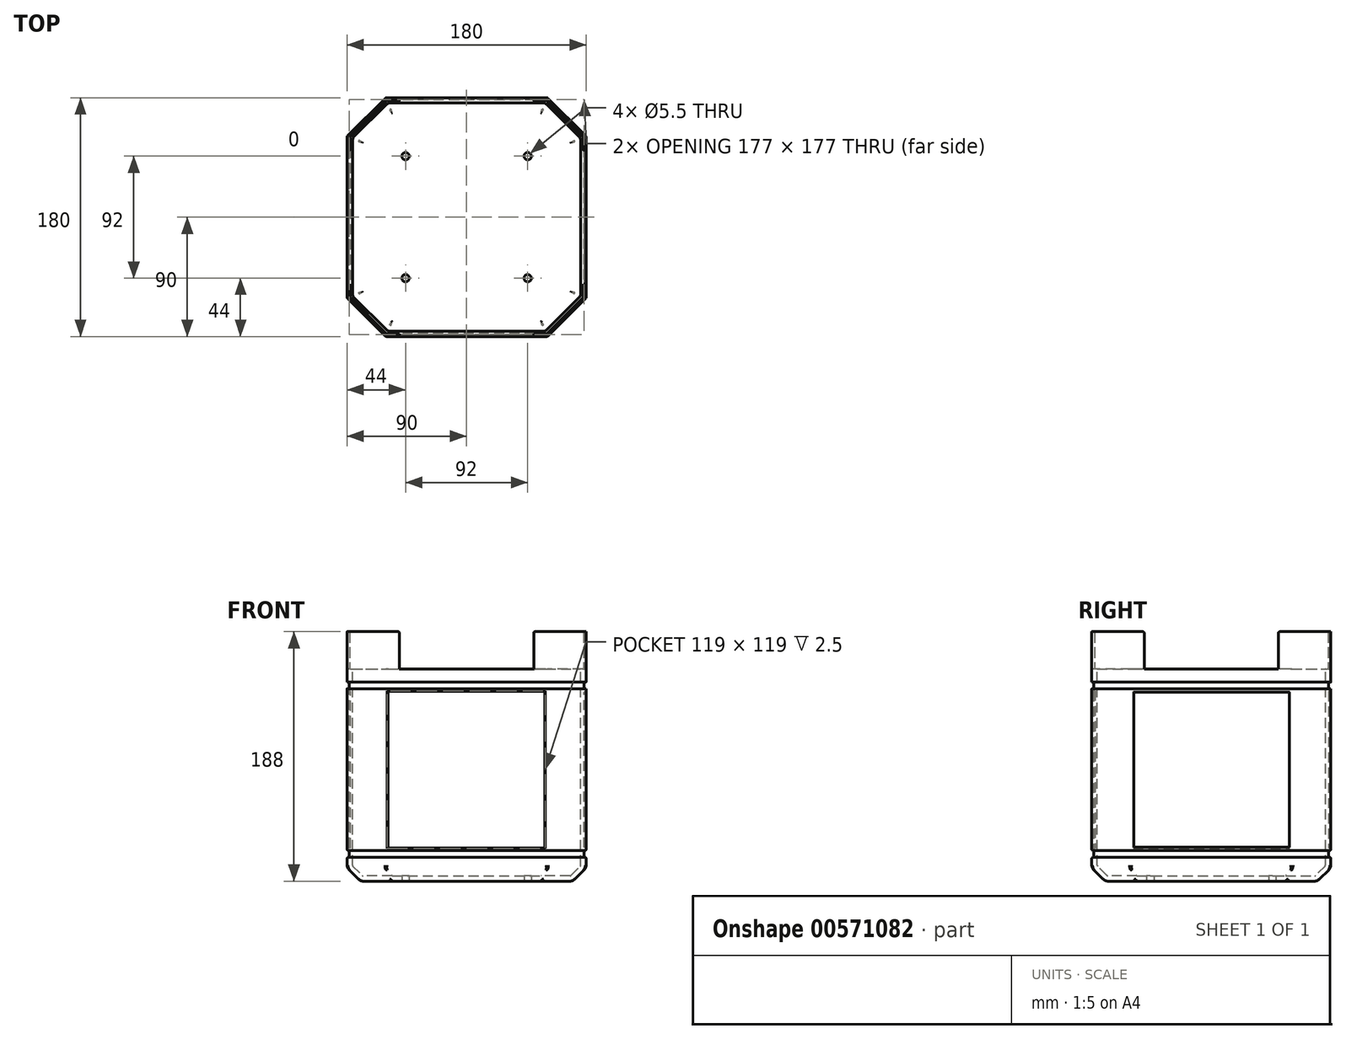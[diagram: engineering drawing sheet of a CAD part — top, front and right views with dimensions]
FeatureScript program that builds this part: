
annotation { "Feature Type Name" : "Feature", "Feature Type Description" : "" }
export const myFeature = defineFeature(function(context is Context, id is Id, definition is map)
    precondition{}
    {
        {
            var Q0;
            Q0=qCreatedBy(makeId("Top.planeOp"),FACE);
            var sketch = newSketch(context, id + "F0", { "sketchPlane" : qUnion([Q0])});
            skLineSegment(sketch, "E0.bottom", {"start": v(-61, 90) * mm, "end": v(61, 90) * mm});
            skLineSegment(sketch, "E0.top", {"start": v(-61, -90) * mm, "end": v(61, -90) * mm});
            skLineSegment(sketch, "E0.left", {"start": v(-90, 61) * mm, "end": v(-90, -61) * mm});
            skLineSegment(sketch, "E0.right", {"start": v(90, 61) * mm, "end": v(90, -61) * mm});
            skLineSegment(sketch, "E1", {"start": v(0, 156.9) * mm, "end": v(0, -146.72) * mm, "construction": true});
            skLineSegment(sketch, "E2", {"start": v(-149.43, 0) * mm, "end": v(169.81, 0) * mm, "construction": true});
            skLineSegment(sketch, "E3", {"start": v(-90, 61) * mm, "end": v(-61, 90) * mm});
            skLineSegment(sketch, "E4", {"start": v(-90, -61) * mm, "end": v(-61, -90) * mm});
            skLineSegment(sketch, "E5", {"start": v(61, -90) * mm, "end": v(90, -61) * mm});
            skLineSegment(sketch, "E6", {"start": v(61, 90) * mm, "end": v(90, 61) * mm});
            skPoint(sketch, "E7.orphan", {"position": v(-90, 90) * mm});
            skPoint(sketch, "E8.orphan", {"position": v(90, 90) * mm});
            skPoint(sketch, "E9.orphan", {"position": v(90, -90) * mm});
            skPoint(sketch, "E10.orphan", {"position": v(-90, -90) * mm});
            skSolve(sketch);
        }
        {
            var Q0;
            Q0=qSketchRegion(id+"F0",true);
            extrude(context, id + "F1", {"entities" : qUnion([Q0]), "depth" : 160 * mm, "offsetDistance" : 25 * mm});
        }
        {
            var Q0;
            Q0=makeQuery(id+"F1.opExtrude","CAP_EDGE",EDGE,{"disambiguationData":[OSD([sQuery(id+"F0.wireOp",EDGE,"E0.top")])],"isStart":true});
            var Q1;
            Q1=makeQuery(id+"F1.opExtrude","CAP_EDGE",EDGE,{"disambiguationData":[OSD([sQuery(id+"F0.wireOp",EDGE,"E4")])],"isStart":true});
            var Q2;
            Q2=makeQuery(id+"F1.opExtrude","CAP_EDGE",EDGE,{"disambiguationData":[OSD([sQuery(id+"F0.wireOp",EDGE,"E0.left")])],"isStart":true});
            var Q3;
            Q3=makeQuery(id+"F1.opExtrude","CAP_EDGE",EDGE,{"disambiguationData":[OSD([sQuery(id+"F0.wireOp",EDGE,"E3")])],"isStart":true});
            var Q4;
            Q4=makeQuery(id+"F1.opExtrude","CAP_EDGE",EDGE,{"disambiguationData":[OSD([sQuery(id+"F0.wireOp",EDGE,"E0.bottom")])],"isStart":true});
            var Q5;
            Q5=makeQuery(id+"F1.opExtrude","CAP_EDGE",EDGE,{"disambiguationData":[OSD([sQuery(id+"F0.wireOp",EDGE,"E6")])],"isStart":true});
            var Q6;
            Q6=makeQuery(id+"F1.opExtrude","CAP_EDGE",EDGE,{"disambiguationData":[OSD([sQuery(id+"F0.wireOp",EDGE,"E0.right")])],"isStart":true});
            var Q7;
            Q7=makeQuery(id+"F1.opExtrude","CAP_EDGE",EDGE,{"disambiguationData":[OSD([sQuery(id+"F0.wireOp",EDGE,"E5")])],"isStart":true});
            chamfer(context, id + "F2", {"entities" : qUnion([Q0, Q1, Q2, Q3, Q4, Q5, Q6, Q7]), "chamferType" : ChamferType.TWO_OFFSETS, "width1" : 10 * mm, "oppositeDirection" : true, "width2" : 10 * mm, "tangentPropagation" : true});
        }
        {
            var Q0;
            Q0=makeQuery(id+"F1.opExtrude","CAP_FACE",FACE,{"disambiguationData":[OSD([sQuery(id+"F0.wireOp",EDGE,"E0.bottom"),sQuery(id+"F0.wireOp",EDGE,"E0.top"),sQuery(id+"F0.wireOp",EDGE,"E0.left"),sQuery(id+"F0.wireOp",EDGE,"E0.right"),sQuery(id+"F0.wireOp",EDGE,"E3"),sQuery(id+"F0.wireOp",EDGE,"E4"),sQuery(id+"F0.wireOp",EDGE,"E5"),sQuery(id+"F0.wireOp",EDGE,"E6")])],"isStart":false});
            var sketch = newSketch(context, id + "F3", { "sketchPlane" : qUnion([Q0])});
            skLineSegment(sketch, "E11", {"start": v(90, -61) * mm, "end": v(61, -90) * mm});
            skLineSegment(sketch, "E12.0", {"start": v(88, -60.17) * mm, "end": v(60.17, -88) * mm});
            skLineSegment(sketch, "E13", {"start": v(90, -61) * mm, "end": v(90, -90) * mm, "construction": true});
            skLineSegment(sketch, "E14", {"start": v(90, -90) * mm, "end": v(61, -90) * mm, "construction": true});
            skLineSegment(sketch, "E15", {"start": v(90, -61) * mm, "end": v(90, -50.5) * mm});
            skLineSegment(sketch, "E16", {"start": v(61, -90) * mm, "end": v(50.5, -90) * mm});
            skLineSegment(sketch, "E17.0", {"start": v(60.17, -88) * mm, "end": v(50.5, -88) * mm});
            skLineSegment(sketch, "E18.0", {"start": v(88, -60.17) * mm, "end": v(88, -50.5) * mm});
            skLineSegment(sketch, "E19", {"start": v(88, -50.5) * mm, "end": v(90, -50.5) * mm});
            skLineSegment(sketch, "E20", {"start": v(50.5, -88) * mm, "end": v(50.5, -90) * mm});
            skLineSegment(sketch, "E21", {"start": v(104.54, 0) * mm, "end": v(-130.04, 0) * mm, "construction": true});
            skPoint(sketch, "E21.endSnap0", {"position": v(-90, 0) * mm});
            skLineSegment(sketch, "E22", {"start": v(0, 121.87) * mm, "end": v(0, -139.26) * mm, "construction": true});
            skLineSegment(sketch, "E23.MirrorCS", {"start": v(88, 50.5) * mm, "end": v(90, 50.5) * mm});
            skLineSegment(sketch, "E24.MirrorCS", {"start": v(50.5, 88) * mm, "end": v(50.5, 90) * mm});
            skLineSegment(sketch, "E25.MirrorCS", {"start": v(61, 90) * mm, "end": v(50.5, 90) * mm});
            skLineSegment(sketch, "E26.MirrorCS", {"start": v(60.17, 88) * mm, "end": v(50.5, 88) * mm});
            skLineSegment(sketch, "E27.MirrorCS", {"start": v(88, 60.17) * mm, "end": v(88, 50.5) * mm});
            skLineSegment(sketch, "E28.MirrorCS", {"start": v(90, 61) * mm, "end": v(90, 50.5) * mm});
            skLineSegment(sketch, "E29.MirrorCS", {"start": v(90, 61) * mm, "end": v(61, 90) * mm});
            skLineSegment(sketch, "E30.MirrorCS", {"start": v(88, 60.17) * mm, "end": v(60.17, 88) * mm});
            skLineSegment(sketch, "E31.MirrorCS", {"start": v(90, 90) * mm, "end": v(61, 90) * mm, "construction": true});
            skLineSegment(sketch, "E32.MirrorCS", {"start": v(90, 61) * mm, "end": v(90, 90) * mm, "construction": true});
            skLineSegment(sketch, "E33.MirrorCS", {"start": v(-88, 50.5) * mm, "end": v(-90, 50.5) * mm});
            skLineSegment(sketch, "E34.MirrorCS", {"start": v(-50.5, 88) * mm, "end": v(-50.5, 90) * mm});
            skLineSegment(sketch, "E35.MirrorCS", {"start": v(-88, -50.5) * mm, "end": v(-90, -50.5) * mm});
            skLineSegment(sketch, "E36.MirrorCS", {"start": v(-50.5, -88) * mm, "end": v(-50.5, -90) * mm});
            skLineSegment(sketch, "E37.MirrorCS", {"start": v(-61, -90) * mm, "end": v(-50.5, -90) * mm});
            skLineSegment(sketch, "E38.MirrorCS", {"start": v(-88, 60.17) * mm, "end": v(-88, 50.5) * mm});
            skLineSegment(sketch, "E39.MirrorCS", {"start": v(-61, 90) * mm, "end": v(-50.5, 90) * mm});
            skLineSegment(sketch, "E40.MirrorCS", {"start": v(-88, 60.17) * mm, "end": v(-60.17, 88) * mm});
            skLineSegment(sketch, "E41.MirrorCS", {"start": v(-88, -60.17) * mm, "end": v(-88, -50.5) * mm});
            skLineSegment(sketch, "E42.MirrorCS", {"start": v(-90, 61) * mm, "end": v(-61, 90) * mm});
            skLineSegment(sketch, "E43.MirrorCS", {"start": v(-60.17, 88) * mm, "end": v(-50.5, 88) * mm});
            skLineSegment(sketch, "E44.MirrorCS", {"start": v(-90, 61) * mm, "end": v(-90, 50.5) * mm});
            skLineSegment(sketch, "E45.MirrorCS", {"start": v(-90, -61) * mm, "end": v(-90, -50.5) * mm});
            skLineSegment(sketch, "E46.MirrorCS", {"start": v(-60.17, -88) * mm, "end": v(-50.5, -88) * mm});
            skLineSegment(sketch, "E47.MirrorCS", {"start": v(-90, 90) * mm, "end": v(-61, 90) * mm, "construction": true});
            skLineSegment(sketch, "E48.MirrorCS", {"start": v(-90, 61) * mm, "end": v(-90, 90) * mm, "construction": true});
            skLineSegment(sketch, "E49.MirrorCS", {"start": v(-90, -61) * mm, "end": v(-61, -90) * mm});
            skLineSegment(sketch, "E50.MirrorCS", {"start": v(-90, -61) * mm, "end": v(-90, -90) * mm, "construction": true});
            skLineSegment(sketch, "E51.MirrorCS", {"start": v(-90, -90) * mm, "end": v(-61, -90) * mm, "construction": true});
            skLineSegment(sketch, "E52.MirrorCS", {"start": v(-88, -60.17) * mm, "end": v(-60.17, -88) * mm});
            skSolve(sketch);
        }
        {
            var Q0;
            Q0=qSketchRegion(id+"F3",true);
            extrude(context, id + "F4", {"entities" : qUnion([Q0]), "operationType" : NewBodyOperationType.ADD, "depth" : 28 * mm});
        }
        {
            var Q0;
            {var subQ0=sQuery(id+"F0.wireOp",EDGE,"E6");Q0=makeQuery(id+"F2.opChamfer","BLEND_EDGE",EDGE,{"blendedFrom":[makeQuery(id+"F1.opExtrude","CAP_EDGE",EDGE,{"disambiguationData":[OSD([subQ0])],"isStart":true}),makeQuery(id+"F1.opExtrude","SWEPT_FACE",FACE,{"disambiguationData":[OSD([subQ0])]})],"blendedInto":[makeQuery(id+"F1.opExtrude","SWEPT_FACE",FACE,{"disambiguationData":[OSD([subQ0])]})]});}
            var Q1;
            {var subQ0=sQuery(id+"F0.wireOp",EDGE,"E0.right");Q1=makeQuery(id+"F2.opChamfer","BLEND_EDGE",EDGE,{"blendedFrom":[makeQuery(id+"F1.opExtrude","CAP_EDGE",EDGE,{"disambiguationData":[OSD([subQ0])],"isStart":true}),makeQuery(id+"F1.opExtrude","SWEPT_FACE",FACE,{"disambiguationData":[OSD([subQ0])]})],"blendedInto":[makeQuery(id+"F1.opExtrude","SWEPT_FACE",FACE,{"disambiguationData":[OSD([subQ0])]})]});}
            var Q2;
            {var subQ0=sQuery(id+"F0.wireOp",EDGE,"E5");Q2=makeQuery(id+"F2.opChamfer","BLEND_EDGE",EDGE,{"blendedFrom":[makeQuery(id+"F1.opExtrude","CAP_EDGE",EDGE,{"disambiguationData":[OSD([subQ0])],"isStart":true}),makeQuery(id+"F1.opExtrude","SWEPT_FACE",FACE,{"disambiguationData":[OSD([subQ0])]})],"blendedInto":[makeQuery(id+"F1.opExtrude","SWEPT_FACE",FACE,{"disambiguationData":[OSD([subQ0])]})]});}
            var Q3;
            {var subQ0=sQuery(id+"F0.wireOp",EDGE,"E0.top");Q3=makeQuery(id+"F2.opChamfer","BLEND_EDGE",EDGE,{"blendedFrom":[makeQuery(id+"F1.opExtrude","CAP_EDGE",EDGE,{"disambiguationData":[OSD([subQ0])],"isStart":true}),makeQuery(id+"F1.opExtrude","SWEPT_FACE",FACE,{"disambiguationData":[OSD([subQ0])]})],"blendedInto":[makeQuery(id+"F1.opExtrude","SWEPT_FACE",FACE,{"disambiguationData":[OSD([subQ0])]})]});}
            var Q4;
            {var subQ0=sQuery(id+"F0.wireOp",EDGE,"E4");Q4=makeQuery(id+"F2.opChamfer","BLEND_EDGE",EDGE,{"blendedFrom":[makeQuery(id+"F1.opExtrude","CAP_EDGE",EDGE,{"disambiguationData":[OSD([subQ0])],"isStart":true}),makeQuery(id+"F1.opExtrude","SWEPT_FACE",FACE,{"disambiguationData":[OSD([subQ0])]})],"blendedInto":[makeQuery(id+"F1.opExtrude","SWEPT_FACE",FACE,{"disambiguationData":[OSD([subQ0])]})]});}
            var Q5;
            {var subQ0=sQuery(id+"F0.wireOp",EDGE,"E0.left");Q5=makeQuery(id+"F2.opChamfer","BLEND_EDGE",EDGE,{"blendedFrom":[makeQuery(id+"F1.opExtrude","CAP_EDGE",EDGE,{"disambiguationData":[OSD([subQ0])],"isStart":true}),makeQuery(id+"F1.opExtrude","SWEPT_FACE",FACE,{"disambiguationData":[OSD([subQ0])]})],"blendedInto":[makeQuery(id+"F1.opExtrude","SWEPT_FACE",FACE,{"disambiguationData":[OSD([subQ0])]})]});}
            var Q6;
            {var subQ0=sQuery(id+"F0.wireOp",EDGE,"E3");Q6=makeQuery(id+"F2.opChamfer","BLEND_EDGE",EDGE,{"blendedFrom":[makeQuery(id+"F1.opExtrude","CAP_EDGE",EDGE,{"disambiguationData":[OSD([subQ0])],"isStart":true}),makeQuery(id+"F1.opExtrude","SWEPT_FACE",FACE,{"disambiguationData":[OSD([subQ0])]})],"blendedInto":[makeQuery(id+"F1.opExtrude","SWEPT_FACE",FACE,{"disambiguationData":[OSD([subQ0])]})]});}
            var Q7;
            {var subQ0=sQuery(id+"F0.wireOp",EDGE,"E0.bottom");Q7=makeQuery(id+"F2.opChamfer","BLEND_EDGE",EDGE,{"blendedFrom":[makeQuery(id+"F1.opExtrude","CAP_EDGE",EDGE,{"disambiguationData":[OSD([subQ0])],"isStart":true}),makeQuery(id+"F1.opExtrude","SWEPT_FACE",FACE,{"disambiguationData":[OSD([subQ0])]})],"blendedInto":[makeQuery(id+"F1.opExtrude","SWEPT_FACE",FACE,{"disambiguationData":[OSD([subQ0])]})]});}
            fillet(context, id + "F5", {"entities" : qUnion([Q0, Q1, Q2, Q3, Q4, Q5, Q6, Q7]), "radius" : 5 * mm, "tangentPropagation" : true, "allowEdgeOverflow" : false});
        }
        {
            var Q0;
            Q0=makeQuery(id+"F4.boolean.opBoolean","MERGE",EDGE,{"derivedFrom":[makeQuery(id+"F1.opExtrude","SWEPT_EDGE",EDGE,{"disambiguationData":[OSD([sQuery(id+"F0.wireOp",EDGE,"E0.bottom"),sQuery(id+"F0.wireOp",EDGE,"E6")])]}),makeQuery(id+"F4.opExtrude","SWEPT_EDGE",EDGE,{"disambiguationData":[OSD([sQuery(id+"F3.wireOp",EDGE,"E25.MirrorCS"),sQuery(id+"F3.wireOp",EDGE,"E29.MirrorCS")])]})]});
            var Q1;
            Q1=makeQuery(id+"F4.boolean.opBoolean","MERGE",EDGE,{"derivedFrom":[makeQuery(id+"F1.opExtrude","SWEPT_EDGE",EDGE,{"disambiguationData":[OSD([sQuery(id+"F0.wireOp",EDGE,"E0.right"),sQuery(id+"F0.wireOp",EDGE,"E6")])]}),makeQuery(id+"F4.opExtrude","SWEPT_EDGE",EDGE,{"disambiguationData":[OSD([sQuery(id+"F3.wireOp",EDGE,"E28.MirrorCS"),sQuery(id+"F3.wireOp",EDGE,"E29.MirrorCS")])]})]});
            var Q2;
            Q2=makeQuery(id+"F4.boolean.opBoolean","MERGE",EDGE,{"derivedFrom":[makeQuery(id+"F1.opExtrude","SWEPT_EDGE",EDGE,{"disambiguationData":[OSD([sQuery(id+"F0.wireOp",EDGE,"E0.bottom"),sQuery(id+"F0.wireOp",EDGE,"E3")])]}),makeQuery(id+"F4.opExtrude","SWEPT_EDGE",EDGE,{"disambiguationData":[OSD([sQuery(id+"F3.wireOp",EDGE,"E39.MirrorCS"),sQuery(id+"F3.wireOp",EDGE,"E42.MirrorCS")])]})]});
            var Q3;
            Q3=makeQuery(id+"F4.boolean.opBoolean","MERGE",EDGE,{"derivedFrom":[makeQuery(id+"F1.opExtrude","SWEPT_EDGE",EDGE,{"disambiguationData":[OSD([sQuery(id+"F0.wireOp",EDGE,"E0.right"),sQuery(id+"F0.wireOp",EDGE,"E5")])]}),makeQuery(id+"F4.opExtrude","SWEPT_EDGE",EDGE,{"disambiguationData":[OSD([sQuery(id+"F3.wireOp",EDGE,"E11"),sQuery(id+"F3.wireOp",EDGE,"E15")])]})]});
            var Q4;
            Q4=makeQuery(id+"F2.opChamfer","BLEND_EDGE",EDGE,{"blendedFrom":[makeQuery(id+"F1.opExtrude","CAP_EDGE",EDGE,{"disambiguationData":[OSD([sQuery(id+"F0.wireOp",EDGE,"E0.top")])],"isStart":true}),makeQuery(id+"F1.opExtrude","CAP_EDGE",EDGE,{"disambiguationData":[OSD([sQuery(id+"F0.wireOp",EDGE,"E5")])],"isStart":true})],"blendedInto":[]});
            var Q5;
            Q5=makeQuery(id+"F2.opChamfer","BLEND_EDGE",EDGE,{"blendedFrom":[makeQuery(id+"F1.opExtrude","CAP_EDGE",EDGE,{"disambiguationData":[OSD([sQuery(id+"F0.wireOp",EDGE,"E0.top")])],"isStart":true}),makeQuery(id+"F1.opExtrude","CAP_EDGE",EDGE,{"disambiguationData":[OSD([sQuery(id+"F0.wireOp",EDGE,"E4")])],"isStart":true})],"blendedInto":[]});
            var Q6;
            Q6=makeQuery(id+"F2.opChamfer","BLEND_EDGE",EDGE,{"blendedFrom":[makeQuery(id+"F1.opExtrude","CAP_EDGE",EDGE,{"disambiguationData":[OSD([sQuery(id+"F0.wireOp",EDGE,"E0.left")])],"isStart":true}),makeQuery(id+"F1.opExtrude","CAP_EDGE",EDGE,{"disambiguationData":[OSD([sQuery(id+"F0.wireOp",EDGE,"E4")])],"isStart":true})],"blendedInto":[]});
            var Q7;
            Q7=makeQuery(id+"F2.opChamfer","BLEND_EDGE",EDGE,{"blendedFrom":[makeQuery(id+"F1.opExtrude","CAP_EDGE",EDGE,{"disambiguationData":[OSD([sQuery(id+"F0.wireOp",EDGE,"E0.left")])],"isStart":true}),makeQuery(id+"F1.opExtrude","CAP_EDGE",EDGE,{"disambiguationData":[OSD([sQuery(id+"F0.wireOp",EDGE,"E3")])],"isStart":true})],"blendedInto":[]});
            fillet(context, id + "F6", {"entities" : qUnion([Q0, Q1, Q2, Q3, Q4, Q5, Q6, Q7]), "radius" : 2 * mm, "tangentPropagation" : true, "allowEdgeOverflow" : false});
        }
        {
            var Q0;
            {var subQ0=sQuery(id+"F0.wireOp",EDGE,"E0.left");Q0=makeQuery(id+"F2.opChamfer","BLEND_EDGE",EDGE,{"blendedFrom":[makeQuery(id+"F1.opExtrude","CAP_EDGE",EDGE,{"disambiguationData":[OSD([subQ0])],"isStart":true}),makeQuery(id+"F1.opExtrude","CAP_FACE",FACE,{"disambiguationData":[OSD([sQuery(id+"F0.wireOp",EDGE,"E0.bottom"),sQuery(id+"F0.wireOp",EDGE,"E0.top"),subQ0,sQuery(id+"F0.wireOp",EDGE,"E0.right"),sQuery(id+"F0.wireOp",EDGE,"E3"),sQuery(id+"F0.wireOp",EDGE,"E4"),sQuery(id+"F0.wireOp",EDGE,"E5"),sQuery(id+"F0.wireOp",EDGE,"E6")])],"isStart":true})],"blendedInto":[makeQuery(id+"F1.opExtrude","CAP_FACE",FACE,{"disambiguationData":[OSD([sQuery(id+"F0.wireOp",EDGE,"E0.bottom"),sQuery(id+"F0.wireOp",EDGE,"E0.top"),subQ0,sQuery(id+"F0.wireOp",EDGE,"E0.right"),sQuery(id+"F0.wireOp",EDGE,"E3"),sQuery(id+"F0.wireOp",EDGE,"E4"),sQuery(id+"F0.wireOp",EDGE,"E5"),sQuery(id+"F0.wireOp",EDGE,"E6")])],"isStart":true})]});}
            fillet(context, id + "F7", {"entities" : qUnion([Q0]), "radius" : 5 * mm, "tangentPropagation" : true, "allowEdgeOverflow" : false});
        }
        {
            var Q0;
            Q0=makeQuery(id+"F1.opExtrude","CAP_FACE",FACE,{"disambiguationData":[OSD([sQuery(id+"F0.wireOp",EDGE,"E0.bottom"),sQuery(id+"F0.wireOp",EDGE,"E0.top"),sQuery(id+"F0.wireOp",EDGE,"E0.left"),sQuery(id+"F0.wireOp",EDGE,"E0.right"),sQuery(id+"F0.wireOp",EDGE,"E3"),sQuery(id+"F0.wireOp",EDGE,"E4"),sQuery(id+"F0.wireOp",EDGE,"E5"),sQuery(id+"F0.wireOp",EDGE,"E6")])],"isStart":false});
            shell(context, id + "F8", {"entities" : qUnion([Q0]), "thickness" : 4 * mm});
        }
        {
            var Q0;
            Q0=qCreatedBy(makeId("Front.planeOp"),FACE);
            var sketch = newSketch(context, id + "F9", { "sketchPlane" : qUnion([Q0])});
            skLineSegment(sketch, "E53.bottom", {"start": v(124, 145) * mm, "end": v(-129.94, 145) * mm});
            skLineSegment(sketch, "E53.top", {"start": v(124, 150) * mm, "end": v(-129.94, 150) * mm});
            skLineSegment(sketch, "E53.left", {"start": v(124, 145) * mm, "end": v(124, 150) * mm});
            skLineSegment(sketch, "E53.right", {"start": v(-129.94, 145) * mm, "end": v(-129.94, 150) * mm});
            skLineSegment(sketch, "E54.bottom", {"start": v(124, 18) * mm, "end": v(-130.65, 18) * mm});
            skLineSegment(sketch, "E54.top", {"start": v(124, 23) * mm, "end": v(-130.65, 23) * mm});
            skLineSegment(sketch, "E54.left", {"start": v(124, 18) * mm, "end": v(124, 23) * mm});
            skLineSegment(sketch, "E54.right", {"start": v(-130.65, 18) * mm, "end": v(-130.65, 23) * mm});
            skSolve(sketch);
        }
        {
            var Q0;
            Q0=qSketchRegion(id+"F9",true);
            extrude(context, id + "F10", {"entities" : qUnion([Q0]), "operationType" : NewBodyOperationType.REMOVE, "oppositeDirection" : true, "depth" : 180 * mm, "symmetric" : true});
        }
        {
            var Q0;
            Q0=makeQuery(id+"F10.boolean.opBoolean","COPY",FACE,{"derivedFrom":makeQuery(id+"F10.opExtrude","SWEPT_FACE",FACE,{"disambiguationData":[OSD([sQuery(id+"F9.wireOp",EDGE,"E53.bottom")])]})});
            var sketch = newSketch(context, id + "F11", { "sketchPlane" : qUnion([Q0])});
            skLineSegment(sketch, "E55.0", {"start": v(-60.38, -88.5) * mm, "end": v(60.38, -88.5) * mm});
            skLineSegment(sketch, "E55.1", {"start": v(-88.5, -60.38) * mm, "end": v(-60.38, -88.5) * mm});
            skLineSegment(sketch, "E55.2", {"start": v(60.38, -88.5) * mm, "end": v(88.5, -60.38) * mm});
            skLineSegment(sketch, "E55.3", {"start": v(-88.5, 60.38) * mm, "end": v(-88.5, -60.38) * mm});
            skLineSegment(sketch, "E55.4", {"start": v(88.5, -60.38) * mm, "end": v(88.5, 60.38) * mm});
            skLineSegment(sketch, "E55.5", {"start": v(88.5, 60.38) * mm, "end": v(60.38, 88.5) * mm});
            skLineSegment(sketch, "E55.6", {"start": v(60.38, 88.5) * mm, "end": v(-60.38, 88.5) * mm});
            skLineSegment(sketch, "E55.7", {"start": v(-60.38, 88.5) * mm, "end": v(-88.5, 60.38) * mm});
            skLineSegment(sketch, "E56.0", {"start": v(-59.34, 86) * mm, "end": v(-59.34, 86) * mm});
            skLineSegment(sketch, "E56.2", {"start": v(-86, 59.34) * mm, "end": v(-86, -59.34) * mm});
            skLineSegment(sketch, "E56.4", {"start": v(-59.34, 86) * mm, "end": v(59.34, 86) * mm});
            skLineSegment(sketch, "E56.6", {"start": v(59.34, 86) * mm, "end": v(59.34, 86) * mm});
            skLineSegment(sketch, "E56.8", {"start": v(86, 59.34) * mm, "end": v(86, -59.34) * mm});
            skLineSegment(sketch, "E56.10", {"start": v(59.34, -86) * mm, "end": v(59.34, -86) * mm});
            skLineSegment(sketch, "E56.12", {"start": v(-59.34, -86) * mm, "end": v(59.34, -86) * mm});
            skLineSegment(sketch, "E56.14", {"start": v(-59.34, -86) * mm, "end": v(-59.34, -86) * mm});
            skLineSegment(sketch, "E57", {"start": v(86, 59.34) * mm, "end": v(59.34, 86) * mm});
            skLineSegment(sketch, "E58", {"start": v(-59.34, 86) * mm, "end": v(-86, 59.34) * mm});
            skLineSegment(sketch, "E59", {"start": v(-59.34, -86) * mm, "end": v(-86, -59.34) * mm});
            skLineSegment(sketch, "E60", {"start": v(86, -59.34) * mm, "end": v(59.34, -86) * mm});
            skSolve(sketch);
        }
        {
            var Q0;
            Q0=qSketchRegion(id+"F11",true);
            var Q1;
            Q1=makeQuery(id+"F10.boolean.opBoolean","COPY",FACE,{"derivedFrom":makeQuery(id+"F10.opExtrude","SWEPT_FACE",FACE,{"disambiguationData":[OSD([sQuery(id+"F9.wireOp",EDGE,"E54.bottom")])]})});
            extrude(context, id + "F12", {"entities" : qUnion([Q0]), "operationType" : NewBodyOperationType.ADD, "depth" : 10 * mm, "hasSecondDirection" : true, "secondDirectionBound" : BoundingType.UP_TO_SURFACE, "secondDirectionOppositeDirection" : true, "secondDirectionBoundEntityFace" : qUnion([Q1]), "secondDirectionDepth" : 25 * mm, "offsetDistance" : 25 * mm});
        }
        {
            var Q0;
            {var subQ0=sQuery(id+"F11.wireOp",EDGE,"E55.7");var subQ1=sQuery(id+"F11.wireOp",EDGE,"E55.3");Q0=makeQuery(id+"F12.boolean.opBoolean","SPLIT",EDGE,{"disambiguationData":[TD([makeQuery(id+"F10.boolean.opBoolean","COPY",FACE,{"derivedFrom":makeQuery(id+"F10.opExtrude","SWEPT_FACE",FACE,{"disambiguationData":[OSD([sQuery(id+"F9.wireOp",EDGE,"E53.bottom")])]})})])],"derivedFrom":makeQuery(id+"F12.opExtrude","SWEPT_EDGE",EDGE,{"disambiguationData":[OSD([subQ1,subQ0])]})});}
            var Q1;
            {var subQ0=sQuery(id+"F11.wireOp",EDGE,"E55.7");var subQ1=sQuery(id+"F11.wireOp",EDGE,"E55.6");Q1=makeQuery(id+"F12.boolean.opBoolean","SPLIT",EDGE,{"disambiguationData":[TD([makeQuery(id+"F10.boolean.opBoolean","COPY",FACE,{"derivedFrom":makeQuery(id+"F10.opExtrude","SWEPT_FACE",FACE,{"disambiguationData":[OSD([sQuery(id+"F9.wireOp",EDGE,"E53.bottom")])]})})])],"derivedFrom":makeQuery(id+"F12.opExtrude","SWEPT_EDGE",EDGE,{"disambiguationData":[OSD([subQ1,subQ0])]})});}
            var Q2;
            {var subQ0=sQuery(id+"F11.wireOp",EDGE,"E55.5");var subQ1=sQuery(id+"F11.wireOp",EDGE,"E55.6");Q2=makeQuery(id+"F12.boolean.opBoolean","SPLIT",EDGE,{"disambiguationData":[TD([makeQuery(id+"F10.boolean.opBoolean","COPY",FACE,{"derivedFrom":makeQuery(id+"F10.opExtrude","SWEPT_FACE",FACE,{"disambiguationData":[OSD([sQuery(id+"F9.wireOp",EDGE,"E53.bottom")])]})})])],"derivedFrom":makeQuery(id+"F12.opExtrude","SWEPT_EDGE",EDGE,{"disambiguationData":[OSD([subQ0,subQ1])]})});}
            var Q3;
            {var subQ0=sQuery(id+"F11.wireOp",EDGE,"E55.5");var subQ1=sQuery(id+"F11.wireOp",EDGE,"E55.6");Q3=makeQuery(id+"F12.boolean.opBoolean","SPLIT",EDGE,{"disambiguationData":[TD([makeQuery(id+"F10.boolean.opBoolean","COPY",FACE,{"derivedFrom":makeQuery(id+"F10.opExtrude","SWEPT_FACE",FACE,{"disambiguationData":[OSD([sQuery(id+"F9.wireOp",EDGE,"Me13D1SK-nVIm-EUZ4-u9ei-o20qw3bNrjn4.bottom")])]})})])],"derivedFrom":makeQuery(id+"F12.opExtrude","SWEPT_EDGE",EDGE,{"disambiguationData":[OSD([subQ0,subQ1])]})});}
            var Q4;
            {var subQ0=sQuery(id+"F11.wireOp",EDGE,"E55.6");var subQ1=sQuery(id+"F11.wireOp",EDGE,"E55.7");Q4=makeQuery(id+"F12.boolean.opBoolean","SPLIT",EDGE,{"disambiguationData":[TD([makeQuery(id+"F10.boolean.opBoolean","COPY",FACE,{"derivedFrom":makeQuery(id+"F10.opExtrude","SWEPT_FACE",FACE,{"disambiguationData":[OSD([sQuery(id+"F9.wireOp",EDGE,"Me13D1SK-nVIm-EUZ4-u9ei-o20qw3bNrjn4.bottom")])]})})])],"derivedFrom":makeQuery(id+"F12.opExtrude","SWEPT_EDGE",EDGE,{"disambiguationData":[OSD([subQ0,subQ1])]})});}
            var Q5;
            {var subQ0=sQuery(id+"F11.wireOp",EDGE,"E55.3");var subQ1=sQuery(id+"F11.wireOp",EDGE,"E55.7");Q5=makeQuery(id+"F12.boolean.opBoolean","SPLIT",EDGE,{"disambiguationData":[TD([makeQuery(id+"F10.boolean.opBoolean","COPY",FACE,{"derivedFrom":makeQuery(id+"F10.opExtrude","SWEPT_FACE",FACE,{"disambiguationData":[OSD([sQuery(id+"F9.wireOp",EDGE,"Me13D1SK-nVIm-EUZ4-u9ei-o20qw3bNrjn4.bottom")])]})})])],"derivedFrom":makeQuery(id+"F12.opExtrude","SWEPT_EDGE",EDGE,{"disambiguationData":[OSD([subQ0,subQ1])]})});}
            var Q6;
            {var subQ0=sQuery(id+"F11.wireOp",EDGE,"E55.5");var subQ1=sQuery(id+"F11.wireOp",EDGE,"E55.4");Q6=makeQuery(id+"F12.boolean.opBoolean","SPLIT",EDGE,{"disambiguationData":[TD([makeQuery(id+"F10.boolean.opBoolean","COPY",FACE,{"derivedFrom":makeQuery(id+"F10.opExtrude","SWEPT_FACE",FACE,{"disambiguationData":[OSD([sQuery(id+"F9.wireOp",EDGE,"Me13D1SK-nVIm-EUZ4-u9ei-o20qw3bNrjn4.bottom")])]})})])],"derivedFrom":makeQuery(id+"F12.opExtrude","SWEPT_EDGE",EDGE,{"disambiguationData":[OSD([subQ1,subQ0])]})});}
            var Q7;
            {var subQ0=sQuery(id+"F11.wireOp",EDGE,"E55.4");var subQ1=sQuery(id+"F11.wireOp",EDGE,"E55.5");Q7=makeQuery(id+"F12.boolean.opBoolean","SPLIT",EDGE,{"disambiguationData":[TD([makeQuery(id+"F10.boolean.opBoolean","COPY",FACE,{"derivedFrom":makeQuery(id+"F10.opExtrude","SWEPT_FACE",FACE,{"disambiguationData":[OSD([sQuery(id+"F9.wireOp",EDGE,"E53.bottom")])]})})])],"derivedFrom":makeQuery(id+"F12.opExtrude","SWEPT_EDGE",EDGE,{"disambiguationData":[OSD([subQ0,subQ1])]})});}
            var Q8;
            {var subQ0=sQuery(id+"F11.wireOp",EDGE,"E55.2");var subQ1=sQuery(id+"F11.wireOp",EDGE,"E55.4");Q8=makeQuery(id+"F12.boolean.opBoolean","SPLIT",EDGE,{"disambiguationData":[TD([makeQuery(id+"F10.boolean.opBoolean","COPY",FACE,{"derivedFrom":makeQuery(id+"F10.opExtrude","SWEPT_FACE",FACE,{"disambiguationData":[OSD([sQuery(id+"F9.wireOp",EDGE,"E53.bottom")])]})})])],"derivedFrom":makeQuery(id+"F12.opExtrude","SWEPT_EDGE",EDGE,{"disambiguationData":[OSD([subQ0,subQ1])]})});}
            var Q9;
            {var subQ0=sQuery(id+"F11.wireOp",EDGE,"E55.2");var subQ1=sQuery(id+"F11.wireOp",EDGE,"E55.0");Q9=makeQuery(id+"F12.boolean.opBoolean","SPLIT",EDGE,{"disambiguationData":[TD([makeQuery(id+"F10.boolean.opBoolean","COPY",FACE,{"derivedFrom":makeQuery(id+"F10.opExtrude","SWEPT_FACE",FACE,{"disambiguationData":[OSD([sQuery(id+"F9.wireOp",EDGE,"E53.bottom")])]})})])],"derivedFrom":makeQuery(id+"F12.opExtrude","SWEPT_EDGE",EDGE,{"disambiguationData":[OSD([subQ1,subQ0])]})});}
            var Q10;
            {var subQ0=sQuery(id+"F11.wireOp",EDGE,"E55.2");var subQ1=sQuery(id+"F11.wireOp",EDGE,"E55.4");Q10=makeQuery(id+"F12.boolean.opBoolean","SPLIT",EDGE,{"disambiguationData":[TD([makeQuery(id+"F10.boolean.opBoolean","COPY",FACE,{"derivedFrom":makeQuery(id+"F10.opExtrude","SWEPT_FACE",FACE,{"disambiguationData":[OSD([sQuery(id+"F9.wireOp",EDGE,"Me13D1SK-nVIm-EUZ4-u9ei-o20qw3bNrjn4.bottom")])]})})])],"derivedFrom":makeQuery(id+"F12.opExtrude","SWEPT_EDGE",EDGE,{"disambiguationData":[OSD([subQ0,subQ1])]})});}
            var Q11;
            {var subQ0=sQuery(id+"F11.wireOp",EDGE,"E55.0");var subQ1=sQuery(id+"F11.wireOp",EDGE,"E55.2");Q11=makeQuery(id+"F12.boolean.opBoolean","SPLIT",EDGE,{"disambiguationData":[TD([makeQuery(id+"F10.boolean.opBoolean","COPY",FACE,{"derivedFrom":makeQuery(id+"F10.opExtrude","SWEPT_FACE",FACE,{"disambiguationData":[OSD([sQuery(id+"F9.wireOp",EDGE,"Me13D1SK-nVIm-EUZ4-u9ei-o20qw3bNrjn4.bottom")])]})})])],"derivedFrom":makeQuery(id+"F12.opExtrude","SWEPT_EDGE",EDGE,{"disambiguationData":[OSD([subQ0,subQ1])]})});}
            var Q12;
            {var subQ0=sQuery(id+"F11.wireOp",EDGE,"E55.0");var subQ1=sQuery(id+"F11.wireOp",EDGE,"E55.1");Q12=makeQuery(id+"F12.boolean.opBoolean","SPLIT",EDGE,{"disambiguationData":[TD([makeQuery(id+"F10.boolean.opBoolean","COPY",FACE,{"derivedFrom":makeQuery(id+"F10.opExtrude","SWEPT_FACE",FACE,{"disambiguationData":[OSD([sQuery(id+"F9.wireOp",EDGE,"E53.bottom")])]})})])],"derivedFrom":makeQuery(id+"F12.opExtrude","SWEPT_EDGE",EDGE,{"disambiguationData":[OSD([subQ0,subQ1])]})});}
            var Q13;
            {var subQ0=sQuery(id+"F11.wireOp",EDGE,"E55.3");var subQ1=sQuery(id+"F11.wireOp",EDGE,"E55.1");Q13=makeQuery(id+"F12.boolean.opBoolean","SPLIT",EDGE,{"disambiguationData":[TD([makeQuery(id+"F10.boolean.opBoolean","COPY",FACE,{"derivedFrom":makeQuery(id+"F10.opExtrude","SWEPT_FACE",FACE,{"disambiguationData":[OSD([sQuery(id+"F9.wireOp",EDGE,"E53.bottom")])]})})])],"derivedFrom":makeQuery(id+"F12.opExtrude","SWEPT_EDGE",EDGE,{"disambiguationData":[OSD([subQ1,subQ0])]})});}
            var Q14;
            {var subQ0=sQuery(id+"F11.wireOp",EDGE,"E55.1");var subQ1=sQuery(id+"F11.wireOp",EDGE,"E55.0");Q14=makeQuery(id+"F12.boolean.opBoolean","SPLIT",EDGE,{"disambiguationData":[TD([makeQuery(id+"F10.boolean.opBoolean","COPY",FACE,{"derivedFrom":makeQuery(id+"F10.opExtrude","SWEPT_FACE",FACE,{"disambiguationData":[OSD([sQuery(id+"F9.wireOp",EDGE,"Me13D1SK-nVIm-EUZ4-u9ei-o20qw3bNrjn4.bottom")])]})})])],"derivedFrom":makeQuery(id+"F12.opExtrude","SWEPT_EDGE",EDGE,{"disambiguationData":[OSD([subQ1,subQ0])]})});}
            var Q15;
            {var subQ0=sQuery(id+"F11.wireOp",EDGE,"E55.1");var subQ1=sQuery(id+"F11.wireOp",EDGE,"E55.3");Q15=makeQuery(id+"F12.boolean.opBoolean","SPLIT",EDGE,{"disambiguationData":[TD([makeQuery(id+"F10.boolean.opBoolean","COPY",FACE,{"derivedFrom":makeQuery(id+"F10.opExtrude","SWEPT_FACE",FACE,{"disambiguationData":[OSD([sQuery(id+"F9.wireOp",EDGE,"Me13D1SK-nVIm-EUZ4-u9ei-o20qw3bNrjn4.bottom")])]})})])],"derivedFrom":makeQuery(id+"F12.opExtrude","SWEPT_EDGE",EDGE,{"disambiguationData":[OSD([subQ0,subQ1])]})});}
            var Q16;
            {var subQ0=sQuery(id+"F11.wireOp",EDGE,"E55.2");var subQ1=sQuery(id+"F11.wireOp",EDGE,"E55.0");Q16=makeQuery(id+"F12.boolean.opBoolean","SPLIT",EDGE,{"disambiguationData":[TD([makeQuery(id+"F10.boolean.opBoolean","COPY",FACE,{"derivedFrom":makeQuery(id+"F10.opExtrude","SWEPT_FACE",FACE,{"disambiguationData":[OSD([sQuery(id+"F9.wireOp",EDGE,"E54.bottom")])]})})])],"derivedFrom":makeQuery(id+"F12.opExtrude","SWEPT_EDGE",EDGE,{"disambiguationData":[OSD([subQ1,subQ0])]})});}
            var Q17;
            {var subQ0=sQuery(id+"F11.wireOp",EDGE,"E55.2");var subQ1=sQuery(id+"F11.wireOp",EDGE,"E55.4");Q17=makeQuery(id+"F12.boolean.opBoolean","SPLIT",EDGE,{"disambiguationData":[TD([makeQuery(id+"F10.boolean.opBoolean","COPY",FACE,{"derivedFrom":makeQuery(id+"F10.opExtrude","SWEPT_FACE",FACE,{"disambiguationData":[OSD([sQuery(id+"F9.wireOp",EDGE,"E54.bottom")])]})})])],"derivedFrom":makeQuery(id+"F12.opExtrude","SWEPT_EDGE",EDGE,{"disambiguationData":[OSD([subQ0,subQ1])]})});}
            var Q18;
            {var subQ0=sQuery(id+"F11.wireOp",EDGE,"E55.0");var subQ1=sQuery(id+"F11.wireOp",EDGE,"E55.1");Q18=makeQuery(id+"F12.boolean.opBoolean","SPLIT",EDGE,{"disambiguationData":[TD([makeQuery(id+"F10.boolean.opBoolean","COPY",FACE,{"derivedFrom":makeQuery(id+"F10.opExtrude","SWEPT_FACE",FACE,{"disambiguationData":[OSD([sQuery(id+"F9.wireOp",EDGE,"E54.bottom")])]})})])],"derivedFrom":makeQuery(id+"F12.opExtrude","SWEPT_EDGE",EDGE,{"disambiguationData":[OSD([subQ0,subQ1])]})});}
            var Q19;
            {var subQ0=sQuery(id+"F11.wireOp",EDGE,"E55.3");var subQ1=sQuery(id+"F11.wireOp",EDGE,"E55.1");Q19=makeQuery(id+"F12.boolean.opBoolean","SPLIT",EDGE,{"disambiguationData":[TD([makeQuery(id+"F10.boolean.opBoolean","COPY",FACE,{"derivedFrom":makeQuery(id+"F10.opExtrude","SWEPT_FACE",FACE,{"disambiguationData":[OSD([sQuery(id+"F9.wireOp",EDGE,"E54.bottom")])]})})])],"derivedFrom":makeQuery(id+"F12.opExtrude","SWEPT_EDGE",EDGE,{"disambiguationData":[OSD([subQ1,subQ0])]})});}
            var Q20;
            {var subQ0=sQuery(id+"F11.wireOp",EDGE,"E55.7");var subQ1=sQuery(id+"F11.wireOp",EDGE,"E55.3");Q20=makeQuery(id+"F12.boolean.opBoolean","SPLIT",EDGE,{"disambiguationData":[TD([makeQuery(id+"F10.boolean.opBoolean","COPY",FACE,{"derivedFrom":makeQuery(id+"F10.opExtrude","SWEPT_FACE",FACE,{"disambiguationData":[OSD([sQuery(id+"F9.wireOp",EDGE,"E54.bottom")])]})})])],"derivedFrom":makeQuery(id+"F12.opExtrude","SWEPT_EDGE",EDGE,{"disambiguationData":[OSD([subQ1,subQ0])]})});}
            var Q21;
            {var subQ0=sQuery(id+"F11.wireOp",EDGE,"E55.7");var subQ1=sQuery(id+"F11.wireOp",EDGE,"E55.6");Q21=makeQuery(id+"F12.boolean.opBoolean","SPLIT",EDGE,{"disambiguationData":[TD([makeQuery(id+"F10.boolean.opBoolean","COPY",FACE,{"derivedFrom":makeQuery(id+"F10.opExtrude","SWEPT_FACE",FACE,{"disambiguationData":[OSD([sQuery(id+"F9.wireOp",EDGE,"E54.bottom")])]})})])],"derivedFrom":makeQuery(id+"F12.opExtrude","SWEPT_EDGE",EDGE,{"disambiguationData":[OSD([subQ1,subQ0])]})});}
            var Q22;
            {var subQ0=sQuery(id+"F11.wireOp",EDGE,"E55.5");var subQ1=sQuery(id+"F11.wireOp",EDGE,"E55.6");Q22=makeQuery(id+"F12.boolean.opBoolean","SPLIT",EDGE,{"disambiguationData":[TD([makeQuery(id+"F10.boolean.opBoolean","COPY",FACE,{"derivedFrom":makeQuery(id+"F10.opExtrude","SWEPT_FACE",FACE,{"disambiguationData":[OSD([sQuery(id+"F9.wireOp",EDGE,"E54.bottom")])]})})])],"derivedFrom":makeQuery(id+"F12.opExtrude","SWEPT_EDGE",EDGE,{"disambiguationData":[OSD([subQ0,subQ1])]})});}
            var Q23;
            {var subQ0=sQuery(id+"F11.wireOp",EDGE,"E55.4");var subQ1=sQuery(id+"F11.wireOp",EDGE,"E55.5");Q23=makeQuery(id+"F12.boolean.opBoolean","SPLIT",EDGE,{"disambiguationData":[TD([makeQuery(id+"F10.boolean.opBoolean","COPY",FACE,{"derivedFrom":makeQuery(id+"F10.opExtrude","SWEPT_FACE",FACE,{"disambiguationData":[OSD([sQuery(id+"F9.wireOp",EDGE,"E54.bottom")])]})})])],"derivedFrom":makeQuery(id+"F12.opExtrude","SWEPT_EDGE",EDGE,{"disambiguationData":[OSD([subQ0,subQ1])]})});}
            fillet(context, id + "F13", {"entities" : qUnion([Q0, Q1, Q2, Q3, Q4, Q5, Q6, Q7, Q8, Q9, Q10, Q11, Q12, Q13, Q14, Q15, Q16, Q17, Q18, Q19, Q20, Q21, Q22, Q23]), "radius" : 2 * mm, "tangentPropagation" : true, "allowEdgeOverflow" : false});
        }
        {
            var Q0;
            Q0=makeQuery(id+"F1.opExtrude","CAP_FACE",FACE,{"disambiguationData":[OSD([sQuery(id+"F0.wireOp",EDGE,"E0.bottom"),sQuery(id+"F0.wireOp",EDGE,"E0.top"),sQuery(id+"F0.wireOp",EDGE,"E0.left"),sQuery(id+"F0.wireOp",EDGE,"E0.right"),sQuery(id+"F0.wireOp",EDGE,"E3"),sQuery(id+"F0.wireOp",EDGE,"E4"),sQuery(id+"F0.wireOp",EDGE,"E5"),sQuery(id+"F0.wireOp",EDGE,"E6")])],"isStart":true});
            var sketch = newSketch(context, id + "F14", { "sketchPlane" : qUnion([Q0])});
            skLineSegment(sketch, "E61", {"start": v(0, 77.93) * mm, "end": v(0, -77.93) * mm, "construction": true});
            skLineSegment(sketch, "E62", {"start": v(-77.93, 0) * mm, "end": v(77.93, 0) * mm, "construction": true});
            skLineSegment(sketch, "E63", {"start": v(-66.96, -66.96) * mm, "end": v(66.96, 66.96) * mm, "construction": true});
            skLineSegment(sketch, "E64", {"start": v(-66.96, 66.96) * mm, "end": v(66.96, -66.96) * mm, "construction": true});
            skCircle(sketch, "E65", {"center": v(-46, -46) * mm, "radius": 2.75 * mm});
            skCircle(sketch, "E66", {"center": v(-46, 46) * mm, "radius": 2.75 * mm});
            skCircle(sketch, "E67", {"center": v(46, 46) * mm, "radius": 2.75 * mm});
            skCircle(sketch, "E68", {"center": v(46, -46) * mm, "radius": 2.75 * mm});
            skSolve(sketch);
        }
        {
            var Q0;
            Q0=qSketchRegion(id+"F14",true);
            extrude(context, id + "F15", {"entities" : qUnion([Q0]), "operationType" : NewBodyOperationType.REMOVE, "oppositeDirection" : true, "depth" : 25 * mm});
        }
        {
            var Q0;
            Q0=makeQuery(id+"F4.opExtrude","SWEPT_EDGE",EDGE,{"disambiguationData":[OSD([sQuery(id+"F3.wireOp",EDGE,"E41.MirrorCS"),sQuery(id+"F3.wireOp",EDGE,"E52.MirrorCS")])]});
            var Q1;
            Q1=makeQuery(id+"F4.opExtrude","SWEPT_EDGE",EDGE,{"disambiguationData":[OSD([sQuery(id+"F3.wireOp",EDGE,"E46.MirrorCS"),sQuery(id+"F3.wireOp",EDGE,"E52.MirrorCS")])]});
            var Q2;
            Q2=makeQuery(id+"F4.opExtrude","SWEPT_EDGE",EDGE,{"disambiguationData":[OSD([sQuery(id+"F3.wireOp",EDGE,"E12.0"),sQuery(id+"F3.wireOp",EDGE,"E18.0")])]});
            var Q3;
            Q3=makeQuery(id+"F4.opExtrude","SWEPT_EDGE",EDGE,{"disambiguationData":[OSD([sQuery(id+"F3.wireOp",EDGE,"E12.0"),sQuery(id+"F3.wireOp",EDGE,"E17.0")])]});
            var Q4;
            Q4=makeQuery(id+"F4.opExtrude","SWEPT_EDGE",EDGE,{"disambiguationData":[OSD([sQuery(id+"F3.wireOp",EDGE,"E27.MirrorCS"),sQuery(id+"F3.wireOp",EDGE,"E30.MirrorCS")])]});
            var Q5;
            Q5=makeQuery(id+"F4.opExtrude","SWEPT_EDGE",EDGE,{"disambiguationData":[OSD([sQuery(id+"F3.wireOp",EDGE,"E26.MirrorCS"),sQuery(id+"F3.wireOp",EDGE,"E30.MirrorCS")])]});
            var Q6;
            Q6=makeQuery(id+"F4.opExtrude","SWEPT_EDGE",EDGE,{"disambiguationData":[OSD([sQuery(id+"F3.wireOp",EDGE,"E43.MirrorCS"),sQuery(id+"F3.wireOp",EDGE,"E40.MirrorCS")])]});
            var Q7;
            Q7=makeQuery(id+"F4.opExtrude","SWEPT_EDGE",EDGE,{"disambiguationData":[OSD([sQuery(id+"F3.wireOp",EDGE,"E38.MirrorCS"),sQuery(id+"F3.wireOp",EDGE,"E40.MirrorCS")])]});
            fillet(context, id + "F16", {"entities" : qUnion([Q0, Q1, Q2, Q3, Q4, Q5, Q6, Q7]), "radius" : 2 * mm, "tangentPropagation" : true, "allowEdgeOverflow" : false});
        }
        {
            var Q0;
            Q0=makeQuery(id+"F4.opExtrude","CAP_EDGE",EDGE,{"disambiguationData":[OSD([sQuery(id+"F3.wireOp",EDGE,"E35.MirrorCS")])],"isStart":false});
            var Q1;
            Q1=makeQuery(id+"F4.opExtrude","CAP_EDGE",EDGE,{"disambiguationData":[OSD([sQuery(id+"F3.wireOp",EDGE,"E36.MirrorCS")])],"isStart":false});
            var Q2;
            Q2=makeQuery(id+"F4.opExtrude","CAP_EDGE",EDGE,{"disambiguationData":[OSD([sQuery(id+"F3.wireOp",EDGE,"E20")])],"isStart":false});
            var Q3;
            Q3=makeQuery(id+"F4.opExtrude","CAP_EDGE",EDGE,{"disambiguationData":[OSD([sQuery(id+"F3.wireOp",EDGE,"E19")])],"isStart":false});
            var Q4;
            Q4=makeQuery(id+"F4.opExtrude","CAP_EDGE",EDGE,{"disambiguationData":[OSD([sQuery(id+"F3.wireOp",EDGE,"E23.MirrorCS")])],"isStart":false});
            var Q5;
            Q5=makeQuery(id+"F4.opExtrude","CAP_EDGE",EDGE,{"disambiguationData":[OSD([sQuery(id+"F3.wireOp",EDGE,"E24.MirrorCS")])],"isStart":false});
            var Q6;
            Q6=makeQuery(id+"F4.opExtrude","CAP_EDGE",EDGE,{"disambiguationData":[OSD([sQuery(id+"F3.wireOp",EDGE,"E34.MirrorCS")])],"isStart":false});
            var Q7;
            Q7=makeQuery(id+"F4.opExtrude","CAP_EDGE",EDGE,{"disambiguationData":[OSD([sQuery(id+"F3.wireOp",EDGE,"E33.MirrorCS")])],"isStart":false});
            var Q8;
            Q8=makeQuery(id+"F10.boolean.opBoolean","COPY",EDGE,{"derivedFrom":makeQuery(id+"F10.opExtrude","CAP_EDGE",EDGE,{"disambiguationData":[OSD([sQuery(id+"F9.wireOp",EDGE,"E53.top")])],"isStart":false})});
            var Q9;
            Q9=makeQuery(id+"F10.boolean.opBoolean","COPY",EDGE,{"derivedFrom":makeQuery(id+"F10.opExtrude","CAP_EDGE",EDGE,{"disambiguationData":[OSD([sQuery(id+"F9.wireOp",EDGE,"E53.bottom")])],"isStart":false})});
            var Q10;
            Q10=makeQuery(id+"F10.boolean.opBoolean","COPY",EDGE,{"derivedFrom":makeQuery(id+"F10.opExtrude","CAP_EDGE",EDGE,{"disambiguationData":[OSD([sQuery(id+"F9.wireOp",EDGE,"Me13D1SK-nVIm-EUZ4-u9ei-o20qw3bNrjn4.bottom")])],"isStart":false})});
            var Q11;
            Q11=makeQuery(id+"F10.boolean.opBoolean","COPY",EDGE,{"derivedFrom":makeQuery(id+"F10.opExtrude","CAP_EDGE",EDGE,{"disambiguationData":[OSD([sQuery(id+"F9.wireOp",EDGE,"Me13D1SK-nVIm-EUZ4-u9ei-o20qw3bNrjn4.top")])],"isStart":false})});
            var Q12;
            Q12=makeQuery(id+"F4.opExtrude","CAP_EDGE",EDGE,{"disambiguationData":[OSD([sQuery(id+"F3.wireOp",EDGE,"E36.MirrorCS")])],"isStart":true});
            var Q13;
            Q13=makeQuery(id+"F4.opExtrude","CAP_EDGE",EDGE,{"disambiguationData":[OSD([sQuery(id+"F3.wireOp",EDGE,"E20")])],"isStart":true});
            var Q14;
            Q14=makeQuery(id+"F4.opExtrude","CAP_EDGE",EDGE,{"disambiguationData":[OSD([sQuery(id+"F3.wireOp",EDGE,"E19")])],"isStart":true});
            var Q15;
            Q15=makeQuery(id+"F4.opExtrude","CAP_EDGE",EDGE,{"disambiguationData":[OSD([sQuery(id+"F3.wireOp",EDGE,"E23.MirrorCS")])],"isStart":true});
            var Q16;
            Q16=makeQuery(id+"F4.opExtrude","CAP_EDGE",EDGE,{"disambiguationData":[OSD([sQuery(id+"F3.wireOp",EDGE,"E35.MirrorCS")])],"isStart":true});
            var Q17;
            Q17=makeQuery(id+"F4.opExtrude","CAP_EDGE",EDGE,{"disambiguationData":[OSD([sQuery(id+"F3.wireOp",EDGE,"E33.MirrorCS")])],"isStart":true});
            var Q18;
            Q18=makeQuery(id+"F4.opExtrude","CAP_EDGE",EDGE,{"disambiguationData":[OSD([sQuery(id+"F3.wireOp",EDGE,"E34.MirrorCS")])],"isStart":true});
            var Q19;
            Q19=makeQuery(id+"F4.opExtrude","CAP_EDGE",EDGE,{"disambiguationData":[OSD([sQuery(id+"F3.wireOp",EDGE,"E24.MirrorCS")])],"isStart":true});
            var Q20;
            Q20=makeQuery(id+"F10.boolean.opBoolean","INTERSECT",EDGE,{"derivedFrom":[makeQuery(id+"F6.opFillet","BLEND_FACE",FACE,{"disambiguationData":[OSD([sQuery(id+"F0.wireOp",EDGE,"E0.bottom"),sQuery(id+"F0.wireOp",EDGE,"E6"),sQuery(id+"F3.wireOp",EDGE,"E25.MirrorCS"),sQuery(id+"F3.wireOp",EDGE,"E29.MirrorCS")])]}),makeQuery(id+"F10.opExtrude","SWEPT_FACE",FACE,{"disambiguationData":[OSD([sQuery(id+"F9.wireOp",EDGE,"E54.top")])]})]});
            var Q21;
            Q21=makeQuery(id+"F10.boolean.opBoolean","INTERSECT",EDGE,{"derivedFrom":[makeQuery(id+"F4.boolean.opBoolean","MERGE",FACE,{"derivedFrom":[makeQuery(id+"F1.opExtrude","SWEPT_FACE",FACE,{"disambiguationData":[OSD([sQuery(id+"F0.wireOp",EDGE,"E6")])]}),makeQuery(id+"F4.opExtrude","SWEPT_FACE",FACE,{"disambiguationData":[OSD([sQuery(id+"F3.wireOp",EDGE,"E29.MirrorCS")])]})]}),makeQuery(id+"F10.opExtrude","SWEPT_FACE",FACE,{"disambiguationData":[OSD([sQuery(id+"F9.wireOp",EDGE,"E54.bottom")])]})]});
            fillet(context, id + "F17", {"entities" : qUnion([Q0, Q1, Q2, Q3, Q4, Q5, Q6, Q7, Q8, Q9, Q10, Q11, Q12, Q13, Q14, Q15, Q16, Q17, Q18, Q19, Q20, Q21]), "radius" : 1 * mm, "tangentPropagation" : true, "allowEdgeOverflow" : false});
        }
        {
            var Q0;
            Q0=makeQuery(id+"F1.opExtrude","CAP_EDGE",EDGE,{"disambiguationData":[OSD([sQuery(id+"F0.wireOp",EDGE,"E0.bottom")])],"isStart":false});
            fillet(context, id + "F18", {"entities" : qUnion([Q0]), "radius" : 1 * mm, "tangentPropagation" : true, "allowEdgeOverflow" : false});
        }
        {
            var Q0;
            {var subQ0=sQuery(id+"F3.wireOp",EDGE,"E28.MirrorCS");var subQ1=sQuery(id+"F3.wireOp",EDGE,"E15");var subQ2=sQuery(id+"F0.wireOp",EDGE,"E0.right");var subQ4=sQuery(id+"F3.wireOp",EDGE,"E29.MirrorCS");var subQ5=sQuery(id+"F0.wireOp",EDGE,"E6");var subQ7=makeQuery(id+"F8.opShell","OFFSET_EDGE",EDGE,{"disambiguationData":[OSD([subQ2,subQ5,subQ1,subQ0,subQ4])]});Q0=makeQuery(id+"F12.boolean.opBoolean","MERGE",EDGE,{"derivedFrom":[makeQuery(id+"F10.boolean.opBoolean","SPLIT",EDGE,{"disambiguationData":[TD([makeQuery(id+"F10.opExtrude","SWEPT_FACE",FACE,{"disambiguationData":[OSD([sQuery(id+"F9.wireOp",EDGE,"Me13D1SK-nVIm-EUZ4-u9ei-o20qw3bNrjn4.top")])]})])],"derivedFrom":subQ7}),makeQuery(id+"F10.boolean.opBoolean","SPLIT",EDGE,{"disambiguationData":[TD([makeQuery(id+"F10.opExtrude","SWEPT_FACE",FACE,{"disambiguationData":[OSD([sQuery(id+"F9.wireOp",EDGE,"E53.bottom")])]})])],"derivedFrom":subQ7}),makeQuery(id+"F10.boolean.opBoolean","SPLIT",EDGE,{"disambiguationData":[TD([makeQuery(id+"F10.opExtrude","SWEPT_FACE",FACE,{"disambiguationData":[OSD([sQuery(id+"F9.wireOp",EDGE,"Me13D1SK-nVIm-EUZ4-u9ei-o20qw3bNrjn4.bottom")])]})])],"derivedFrom":subQ7}),makeQuery(id+"F12.opExtrude","SWEPT_EDGE",EDGE,{"disambiguationData":[OSD([sQuery(id+"F11.wireOp",EDGE,"E56.8"),sQuery(id+"F11.wireOp",EDGE,"E57")])]})]});}
            var Q1;
            {var subQ0=sQuery(id+"F3.wireOp",EDGE,"E39.MirrorCS");var subQ1=sQuery(id+"F3.wireOp",EDGE,"E25.MirrorCS");var subQ2=sQuery(id+"F0.wireOp",EDGE,"E0.bottom");var subQ4=sQuery(id+"F3.wireOp",EDGE,"E29.MirrorCS");var subQ5=sQuery(id+"F0.wireOp",EDGE,"E6");var subQ7=makeQuery(id+"F8.opShell","OFFSET_EDGE",EDGE,{"disambiguationData":[OSD([subQ2,subQ5,subQ1,subQ4,subQ0])]});Q1=makeQuery(id+"F12.boolean.opBoolean","MERGE",EDGE,{"derivedFrom":[makeQuery(id+"F10.boolean.opBoolean","SPLIT",EDGE,{"disambiguationData":[TD([makeQuery(id+"F10.opExtrude","SWEPT_FACE",FACE,{"disambiguationData":[OSD([sQuery(id+"F9.wireOp",EDGE,"Me13D1SK-nVIm-EUZ4-u9ei-o20qw3bNrjn4.top")])]})])],"derivedFrom":subQ7}),makeQuery(id+"F10.boolean.opBoolean","SPLIT",EDGE,{"disambiguationData":[TD([makeQuery(id+"F10.opExtrude","SWEPT_FACE",FACE,{"disambiguationData":[OSD([sQuery(id+"F9.wireOp",EDGE,"E53.bottom")])]})])],"derivedFrom":subQ7}),makeQuery(id+"F10.boolean.opBoolean","SPLIT",EDGE,{"disambiguationData":[TD([makeQuery(id+"F10.opExtrude","SWEPT_FACE",FACE,{"disambiguationData":[OSD([sQuery(id+"F9.wireOp",EDGE,"Me13D1SK-nVIm-EUZ4-u9ei-o20qw3bNrjn4.bottom")])]})])],"derivedFrom":subQ7}),makeQuery(id+"F12.opExtrude","SWEPT_EDGE",EDGE,{"disambiguationData":[OSD([sQuery(id+"F11.wireOp",EDGE,"E56.4"),sQuery(id+"F11.wireOp",EDGE,"E57")])]})]});}
            var Q2;
            {var subQ0=sQuery(id+"F3.wireOp",EDGE,"E28.MirrorCS");var subQ1=sQuery(id+"F3.wireOp",EDGE,"E15");var subQ2=sQuery(id+"F0.wireOp",EDGE,"E0.right");var subQ4=sQuery(id+"F3.wireOp",EDGE,"E11");var subQ5=sQuery(id+"F0.wireOp",EDGE,"E5");var subQ7=makeQuery(id+"F8.opShell","OFFSET_EDGE",EDGE,{"disambiguationData":[OSD([subQ2,subQ5,subQ4,subQ1,subQ0])]});Q2=makeQuery(id+"F12.boolean.opBoolean","MERGE",EDGE,{"derivedFrom":[makeQuery(id+"F10.boolean.opBoolean","SPLIT",EDGE,{"disambiguationData":[TD([makeQuery(id+"F10.opExtrude","SWEPT_FACE",FACE,{"disambiguationData":[OSD([sQuery(id+"F9.wireOp",EDGE,"Me13D1SK-nVIm-EUZ4-u9ei-o20qw3bNrjn4.top")])]})])],"derivedFrom":subQ7}),makeQuery(id+"F10.boolean.opBoolean","SPLIT",EDGE,{"disambiguationData":[TD([makeQuery(id+"F10.opExtrude","SWEPT_FACE",FACE,{"disambiguationData":[OSD([sQuery(id+"F9.wireOp",EDGE,"E53.bottom")])]})])],"derivedFrom":subQ7}),makeQuery(id+"F10.boolean.opBoolean","SPLIT",EDGE,{"disambiguationData":[TD([makeQuery(id+"F10.opExtrude","SWEPT_FACE",FACE,{"disambiguationData":[OSD([sQuery(id+"F9.wireOp",EDGE,"Me13D1SK-nVIm-EUZ4-u9ei-o20qw3bNrjn4.bottom")])]})])],"derivedFrom":subQ7}),makeQuery(id+"F12.opExtrude","SWEPT_EDGE",EDGE,{"disambiguationData":[OSD([sQuery(id+"F11.wireOp",EDGE,"E56.8"),sQuery(id+"F11.wireOp",EDGE,"E60")])]})]});}
            var Q3;
            {var subQ0=sQuery(id+"F3.wireOp",EDGE,"E37.MirrorCS");var subQ1=sQuery(id+"F3.wireOp",EDGE,"E16");var subQ2=sQuery(id+"F0.wireOp",EDGE,"E0.top");var subQ4=sQuery(id+"F3.wireOp",EDGE,"E11");var subQ5=sQuery(id+"F0.wireOp",EDGE,"E5");var subQ7=makeQuery(id+"F8.opShell","OFFSET_EDGE",EDGE,{"disambiguationData":[OSD([subQ2,subQ5,subQ4,subQ1,subQ0])]});Q3=makeQuery(id+"F12.boolean.opBoolean","MERGE",EDGE,{"derivedFrom":[makeQuery(id+"F10.boolean.opBoolean","SPLIT",EDGE,{"disambiguationData":[TD([makeQuery(id+"F10.opExtrude","SWEPT_FACE",FACE,{"disambiguationData":[OSD([sQuery(id+"F9.wireOp",EDGE,"Me13D1SK-nVIm-EUZ4-u9ei-o20qw3bNrjn4.top")])]})])],"derivedFrom":subQ7}),makeQuery(id+"F10.boolean.opBoolean","SPLIT",EDGE,{"disambiguationData":[TD([makeQuery(id+"F10.opExtrude","SWEPT_FACE",FACE,{"disambiguationData":[OSD([sQuery(id+"F9.wireOp",EDGE,"E53.bottom")])]})])],"derivedFrom":subQ7}),makeQuery(id+"F10.boolean.opBoolean","SPLIT",EDGE,{"disambiguationData":[TD([makeQuery(id+"F10.opExtrude","SWEPT_FACE",FACE,{"disambiguationData":[OSD([sQuery(id+"F9.wireOp",EDGE,"Me13D1SK-nVIm-EUZ4-u9ei-o20qw3bNrjn4.bottom")])]})])],"derivedFrom":subQ7}),makeQuery(id+"F12.opExtrude","SWEPT_EDGE",EDGE,{"disambiguationData":[OSD([sQuery(id+"F11.wireOp",EDGE,"E56.12"),sQuery(id+"F11.wireOp",EDGE,"E60")])]})]});}
            var Q4;
            {var subQ0=sQuery(id+"F3.wireOp",EDGE,"E37.MirrorCS");var subQ1=sQuery(id+"F3.wireOp",EDGE,"E16");var subQ2=sQuery(id+"F0.wireOp",EDGE,"E0.top");var subQ4=sQuery(id+"F3.wireOp",EDGE,"E49.MirrorCS");var subQ5=sQuery(id+"F0.wireOp",EDGE,"E4");var subQ7=makeQuery(id+"F8.opShell","OFFSET_EDGE",EDGE,{"disambiguationData":[OSD([subQ2,subQ5,subQ1,subQ0,subQ4])]});Q4=makeQuery(id+"F12.boolean.opBoolean","MERGE",EDGE,{"derivedFrom":[makeQuery(id+"F10.boolean.opBoolean","SPLIT",EDGE,{"disambiguationData":[TD([makeQuery(id+"F10.opExtrude","SWEPT_FACE",FACE,{"disambiguationData":[OSD([sQuery(id+"F9.wireOp",EDGE,"Me13D1SK-nVIm-EUZ4-u9ei-o20qw3bNrjn4.top")])]})])],"derivedFrom":subQ7}),makeQuery(id+"F10.boolean.opBoolean","SPLIT",EDGE,{"disambiguationData":[TD([makeQuery(id+"F10.opExtrude","SWEPT_FACE",FACE,{"disambiguationData":[OSD([sQuery(id+"F9.wireOp",EDGE,"E53.bottom")])]})])],"derivedFrom":subQ7}),makeQuery(id+"F10.boolean.opBoolean","SPLIT",EDGE,{"disambiguationData":[TD([makeQuery(id+"F10.opExtrude","SWEPT_FACE",FACE,{"disambiguationData":[OSD([sQuery(id+"F9.wireOp",EDGE,"Me13D1SK-nVIm-EUZ4-u9ei-o20qw3bNrjn4.bottom")])]})])],"derivedFrom":subQ7}),makeQuery(id+"F12.opExtrude","SWEPT_EDGE",EDGE,{"disambiguationData":[OSD([sQuery(id+"F11.wireOp",EDGE,"E56.12"),sQuery(id+"F11.wireOp",EDGE,"E59")])]})]});}
            var Q5;
            {var subQ0=sQuery(id+"F3.wireOp",EDGE,"E44.MirrorCS");var subQ1=sQuery(id+"F3.wireOp",EDGE,"E45.MirrorCS");var subQ2=sQuery(id+"F0.wireOp",EDGE,"E0.left");var subQ4=sQuery(id+"F3.wireOp",EDGE,"E49.MirrorCS");var subQ5=sQuery(id+"F0.wireOp",EDGE,"E4");var subQ7=makeQuery(id+"F8.opShell","OFFSET_EDGE",EDGE,{"disambiguationData":[OSD([subQ2,subQ5,subQ1,subQ0,subQ4])]});Q5=makeQuery(id+"F12.boolean.opBoolean","MERGE",EDGE,{"derivedFrom":[makeQuery(id+"F10.boolean.opBoolean","SPLIT",EDGE,{"disambiguationData":[TD([makeQuery(id+"F10.opExtrude","SWEPT_FACE",FACE,{"disambiguationData":[OSD([sQuery(id+"F9.wireOp",EDGE,"Me13D1SK-nVIm-EUZ4-u9ei-o20qw3bNrjn4.top")])]})])],"derivedFrom":subQ7}),makeQuery(id+"F10.boolean.opBoolean","SPLIT",EDGE,{"disambiguationData":[TD([makeQuery(id+"F10.opExtrude","SWEPT_FACE",FACE,{"disambiguationData":[OSD([sQuery(id+"F9.wireOp",EDGE,"E53.bottom")])]})])],"derivedFrom":subQ7}),makeQuery(id+"F10.boolean.opBoolean","SPLIT",EDGE,{"disambiguationData":[TD([makeQuery(id+"F10.opExtrude","SWEPT_FACE",FACE,{"disambiguationData":[OSD([sQuery(id+"F9.wireOp",EDGE,"Me13D1SK-nVIm-EUZ4-u9ei-o20qw3bNrjn4.bottom")])]})])],"derivedFrom":subQ7}),makeQuery(id+"F12.opExtrude","SWEPT_EDGE",EDGE,{"disambiguationData":[OSD([sQuery(id+"F11.wireOp",EDGE,"E56.2"),sQuery(id+"F11.wireOp",EDGE,"E59")])]})]});}
            var Q6;
            {var subQ0=sQuery(id+"F3.wireOp",EDGE,"E44.MirrorCS");var subQ1=sQuery(id+"F3.wireOp",EDGE,"E45.MirrorCS");var subQ2=sQuery(id+"F0.wireOp",EDGE,"E0.left");var subQ4=sQuery(id+"F3.wireOp",EDGE,"E42.MirrorCS");var subQ5=sQuery(id+"F0.wireOp",EDGE,"E3");var subQ7=makeQuery(id+"F8.opShell","OFFSET_EDGE",EDGE,{"disambiguationData":[OSD([subQ2,subQ5,subQ1,subQ0,subQ4])]});Q6=makeQuery(id+"F12.boolean.opBoolean","MERGE",EDGE,{"derivedFrom":[makeQuery(id+"F10.boolean.opBoolean","SPLIT",EDGE,{"disambiguationData":[TD([makeQuery(id+"F10.opExtrude","SWEPT_FACE",FACE,{"disambiguationData":[OSD([sQuery(id+"F9.wireOp",EDGE,"Me13D1SK-nVIm-EUZ4-u9ei-o20qw3bNrjn4.top")])]})])],"derivedFrom":subQ7}),makeQuery(id+"F10.boolean.opBoolean","SPLIT",EDGE,{"disambiguationData":[TD([makeQuery(id+"F10.opExtrude","SWEPT_FACE",FACE,{"disambiguationData":[OSD([sQuery(id+"F9.wireOp",EDGE,"E53.bottom")])]})])],"derivedFrom":subQ7}),makeQuery(id+"F10.boolean.opBoolean","SPLIT",EDGE,{"disambiguationData":[TD([makeQuery(id+"F10.opExtrude","SWEPT_FACE",FACE,{"disambiguationData":[OSD([sQuery(id+"F9.wireOp",EDGE,"Me13D1SK-nVIm-EUZ4-u9ei-o20qw3bNrjn4.bottom")])]})])],"derivedFrom":subQ7}),makeQuery(id+"F12.opExtrude","SWEPT_EDGE",EDGE,{"disambiguationData":[OSD([sQuery(id+"F11.wireOp",EDGE,"E56.2"),sQuery(id+"F11.wireOp",EDGE,"E58")])]})]});}
            var Q7;
            {var subQ0=sQuery(id+"F3.wireOp",EDGE,"E39.MirrorCS");var subQ1=sQuery(id+"F3.wireOp",EDGE,"E25.MirrorCS");var subQ2=sQuery(id+"F0.wireOp",EDGE,"E0.bottom");var subQ4=sQuery(id+"F3.wireOp",EDGE,"E42.MirrorCS");var subQ5=sQuery(id+"F0.wireOp",EDGE,"E3");var subQ7=makeQuery(id+"F8.opShell","OFFSET_EDGE",EDGE,{"disambiguationData":[OSD([subQ2,subQ5,subQ1,subQ0,subQ4])]});Q7=makeQuery(id+"F12.boolean.opBoolean","MERGE",EDGE,{"derivedFrom":[makeQuery(id+"F10.boolean.opBoolean","SPLIT",EDGE,{"disambiguationData":[TD([makeQuery(id+"F10.opExtrude","SWEPT_FACE",FACE,{"disambiguationData":[OSD([sQuery(id+"F9.wireOp",EDGE,"Me13D1SK-nVIm-EUZ4-u9ei-o20qw3bNrjn4.top")])]})])],"derivedFrom":subQ7}),makeQuery(id+"F10.boolean.opBoolean","SPLIT",EDGE,{"disambiguationData":[TD([makeQuery(id+"F10.opExtrude","SWEPT_FACE",FACE,{"disambiguationData":[OSD([sQuery(id+"F9.wireOp",EDGE,"E53.bottom")])]})])],"derivedFrom":subQ7}),makeQuery(id+"F10.boolean.opBoolean","SPLIT",EDGE,{"disambiguationData":[TD([makeQuery(id+"F10.opExtrude","SWEPT_FACE",FACE,{"disambiguationData":[OSD([sQuery(id+"F9.wireOp",EDGE,"Me13D1SK-nVIm-EUZ4-u9ei-o20qw3bNrjn4.bottom")])]})])],"derivedFrom":subQ7}),makeQuery(id+"F12.opExtrude","SWEPT_EDGE",EDGE,{"disambiguationData":[OSD([sQuery(id+"F11.wireOp",EDGE,"E56.4"),sQuery(id+"F11.wireOp",EDGE,"E58")])]})]});}
            fillet(context, id + "F19", {"entities" : qUnion([Q0, Q1, Q2, Q3, Q4, Q5, Q6, Q7]), "radius" : 1 * mm, "tangentPropagation" : true, "allowEdgeOverflow" : false});
        }
        {
            var Q0;
            {var subQ0=sQuery(id+"F3.wireOp",EDGE,"E37.MirrorCS");var subQ1=sQuery(id+"F0.wireOp",EDGE,"E0.top");var subQ2=sQuery(id+"F3.wireOp",EDGE,"E16");Q0=makeQuery(id+"F10.boolean.opBoolean","SPLIT",FACE,{"disambiguationData":[TD([makeQuery(id+"F10.opExtrude","SWEPT_FACE",FACE,{"disambiguationData":[OSD([sQuery(id+"F9.wireOp",EDGE,"E53.bottom")])]})])],"derivedFrom":makeQuery(id+"F4.boolean.opBoolean","MERGE",FACE,{"derivedFrom":[makeQuery(id+"F1.opExtrude","SWEPT_FACE",FACE,{"disambiguationData":[OSD([subQ1])]}),makeQuery(id+"F4.opExtrude","SWEPT_FACE",FACE,{"disambiguationData":[OSD([subQ2])]}),makeQuery(id+"F4.opExtrude","SWEPT_FACE",FACE,{"disambiguationData":[OSD([subQ0])]})]})});}
            var sketch = newSketch(context, id + "F20", { "sketchPlane" : qUnion([Q0])});
            skLineSegment(sketch, "E69.bottom", {"start": v(-59.67, 143.5) * mm, "end": v(59.33, 143.5) * mm});
            skLineSegment(sketch, "E69.top", {"start": v(-59.67, 24.5) * mm, "end": v(59.33, 24.5) * mm});
            skLineSegment(sketch, "E69.left", {"start": v(-59.67, 143.5) * mm, "end": v(-59.67, 24.5) * mm});
            skLineSegment(sketch, "E69.right", {"start": v(59.33, 143.5) * mm, "end": v(59.33, 24.5) * mm});
            skSolve(sketch);
        }
        {
            var Q0;
            Q0 = qSketchRegion(id + "F20", true);
            extrude(context, id + "F21", {"entities" : qUnion([Q0]), "operationType" : NewBodyOperationType.REMOVE, "oppositeDirection" : true, "depth" : 2.5 * mm, "offsetDistance" : 25 * mm});
        }
        {
            var Q0;
            Q0=makeQuery(id+"F21.boolean.opBoolean","COPY",FACE,{"derivedFrom":makeQuery(id+"F21.opExtrude","CAP_FACE",FACE,{"disambiguationData":[OSD([sQuery(id+"F20.wireOp",EDGE,"E69.bottom"),sQuery(id+"F20.wireOp",EDGE,"E69.top"),sQuery(id+"F20.wireOp",EDGE,"E69.left"),sQuery(id+"F20.wireOp",EDGE,"E69.right")])],"isStart":false})});
            cPlane(context, id + "F22", {"entities" : qUnion([Q0]), "cplaneType" : CPlaneType.OFFSET, "offset" : 1 * mm, "width" : 150 * mm, "height" : 150 * mm});
        }
        {
            var Q0;
            Q0=qCreatedBy(id+"F22.planeOp",FACE);
            var sketch = newSketch(context, id + "F23", { "sketchPlane" : qUnion([Q0])});
            skLineSegment(sketch, "E70.0", {"start": v(58.83, 143) * mm, "end": v(58.83, 25) * mm});
            skLineSegment(sketch, "E70.1", {"start": v(-59.17, 143) * mm, "end": v(58.83, 143) * mm});
            skLineSegment(sketch, "E70.2", {"start": v(-59.17, 143) * mm, "end": v(-59.17, 25) * mm});
            skLineSegment(sketch, "E70.3", {"start": v(-59.17, 25) * mm, "end": v(58.83, 25) * mm});
            skSolve(sketch);
        }
        {
            var Q0;
            Q0 = qSketchRegion(id + "F23", true);
            extrude(context, id + "F24", {"entities" : qUnion([Q0]), "depth" : 1.5 * mm, "offsetDistance" : 25 * mm});
        }
        {
            var Q0;
            Q0=makeQuery(id+"F24.opExtrude","SWEPT_BODY",BODY,{"disambiguationData":[OSD([sQuery(id+"F23.wireOp",EDGE,"E70.0"),sQuery(id+"F23.wireOp",EDGE,"E70.1"),sQuery(id+"F23.wireOp",EDGE,"E70.2"),sQuery(id+"F23.wireOp",EDGE,"E70.3")])]});
            var Q1;
            Q1=qCreatedBy(makeId("Front.planeOp"),FACE);
            mirror(context, id + "F25", {"entities" : qUnion([Q0]), "mirrorPlane" : qUnion([Q1])});
        }
        {
            var Q0;
            {var subQ0=sQuery(id+"F3.wireOp",EDGE,"E44.MirrorCS");var subQ1=sQuery(id+"F0.wireOp",EDGE,"E0.left");var subQ2=sQuery(id+"F3.wireOp",EDGE,"E45.MirrorCS");Q0=makeQuery(id+"F10.boolean.opBoolean","SPLIT",FACE,{"disambiguationData":[TD([makeQuery(id+"F10.opExtrude","SWEPT_FACE",FACE,{"disambiguationData":[OSD([sQuery(id+"F9.wireOp",EDGE,"E53.bottom")])]})])],"derivedFrom":makeQuery(id+"F4.boolean.opBoolean","MERGE",FACE,{"derivedFrom":[makeQuery(id+"F1.opExtrude","SWEPT_FACE",FACE,{"disambiguationData":[OSD([subQ1])]}),makeQuery(id+"F4.opExtrude","SWEPT_FACE",FACE,{"disambiguationData":[OSD([subQ2])]}),makeQuery(id+"F4.opExtrude","SWEPT_FACE",FACE,{"disambiguationData":[OSD([subQ0])]})]})});}
            var sketch = newSketch(context, id + "F26", { "sketchPlane" : qUnion([Q0])});
            skLineSegment(sketch, "E71.bottom", {"start": v(58.83, 25) * mm, "end": v(-59.17, 25) * mm});
            skLineSegment(sketch, "E71.top", {"start": v(58.83, 143) * mm, "end": v(-59.17, 143) * mm});
            skLineSegment(sketch, "E71.left", {"start": v(58.83, 25) * mm, "end": v(58.83, 143) * mm});
            skLineSegment(sketch, "E71.right", {"start": v(-59.17, 25) * mm, "end": v(-59.17, 143) * mm});
            skSolve(sketch);
        }
        {
            var Q0;
            Q0 = qSketchRegion(id + "F26", true);
            extrude(context, id + "F27", {"entities" : qUnion([Q0]), "operationType" : NewBodyOperationType.REMOVE, "oppositeDirection" : true, "depth" : 2.5 * mm, "offsetDistance" : 25 * mm});
        }
        {
            var Q0;
            Q0=makeQuery(id+"F27.boolean.opBoolean","COPY",FACE,{"derivedFrom":makeQuery(id+"F27.opExtrude","CAP_FACE",FACE,{"disambiguationData":[OSD([sQuery(id+"F26.wireOp",EDGE,"E71.bottom"),sQuery(id+"F26.wireOp",EDGE,"E71.top"),sQuery(id+"F26.wireOp",EDGE,"E71.left"),sQuery(id+"F26.wireOp",EDGE,"E71.right")])],"isStart":false})});
            cPlane(context, id + "F28", {"entities" : qUnion([Q0]), "cplaneType" : CPlaneType.OFFSET, "offset" : 1 * mm, "width" : 150 * mm, "height" : 150 * mm});
        }
        {
            var Q0;
            Q0=qCreatedBy(id+"F28.planeOp",FACE);
            var sketch = newSketch(context, id + "F29", { "sketchPlane" : qUnion([Q0])});
            skLineSegment(sketch, "E72.0", {"start": v(58.33, 25.5) * mm, "end": v(58.33, 142.5) * mm});
            skLineSegment(sketch, "E72.1", {"start": v(58.33, 25.5) * mm, "end": v(-58.67, 25.5) * mm});
            skLineSegment(sketch, "E72.2", {"start": v(-58.67, 25.5) * mm, "end": v(-58.67, 142.5) * mm});
            skLineSegment(sketch, "E72.3", {"start": v(58.33, 142.5) * mm, "end": v(-58.67, 142.5) * mm});
            skSolve(sketch);
        }
        {
            var Q0;
            Q0 = qSketchRegion(id + "F29", true);
            extrude(context, id + "F30", {"entities" : qUnion([Q0]), "depth" : 1.5 * mm, "offsetDistance" : 25 * mm});
        }
        {
            var Q0;
            Q0=makeQuery(id+"F30.opExtrude","SWEPT_BODY",BODY,{"disambiguationData":[OSD([sQuery(id+"F29.wireOp",EDGE,"E72.0"),sQuery(id+"F29.wireOp",EDGE,"E72.1"),sQuery(id+"F29.wireOp",EDGE,"E72.2"),sQuery(id+"F29.wireOp",EDGE,"E72.3")])]});
            var Q1;
            Q1=qCreatedBy(makeId("Right.planeOp"),FACE);
            mirror(context, id + "F31", {"entities" : qUnion([Q0]), "mirrorPlane" : qUnion([Q1])});
        }
    });
